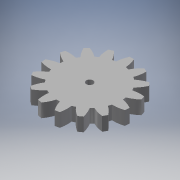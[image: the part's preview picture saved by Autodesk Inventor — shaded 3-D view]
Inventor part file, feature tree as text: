
AUTODESK INVENTOR PART (.ipt)
format: ipt  version: 2018 (Build 220112000, 112)  size: 222,720 bytes
history: native  units: mm (DEFAULTED — no unit token found)
features: sketch x4, extrude x3, plane x3, other x3
ambient origin geometry x8: Origin, YZ Plane, XZ Plane, XY Plane, X Axis, Y Axis, Z Axis, Center Point
bodies: Solid1 (feature_tree)
feature tree (13):
  extrude  "Extrusion1"  Depth=5.0mm TaperAngle=0.0deg
  plane  "Work Plane2"
  plane  "Work Plane8"
  plane  "Work Plane9"
  other  "Stirnzahnrad"
  extrude  "Extrusion2"  Depth=10.0mm TaperAngle=0.0deg
  extrude  "Extrusion3"  TaperAngle=0.0deg  [1 undecoded]
  sketch  "Sketch1"  dims[d0=31.0mm d1=5.0mm d2=0.0mm]
  sketch  "Sketch2"  dims[d3=26.666667mm d4=10.0mm d5=0.0mm]
  other  "Srf1"
  sketch  "Skizze3"  dims[d16=40.0mm d17=0.0mm]
  sketch  "Skizze4"  dims[d34=2.094395mm d39=0.0mm d41=0.0mm d43=40.0mm d46=40.0mm d47=0.0mm d48=0.0mm d49=4.8mm d50=3.0mm d51=0.0mm d52=2.5mm d53=10.0mm d54=0.0mm]
  other  "Flankendurchmesser"
note: 1 required parameter value undecoded (feature->parameter linkage not recoverable at this tier; creation-order binding heuristic only, values carry confidence <= 0.55)
